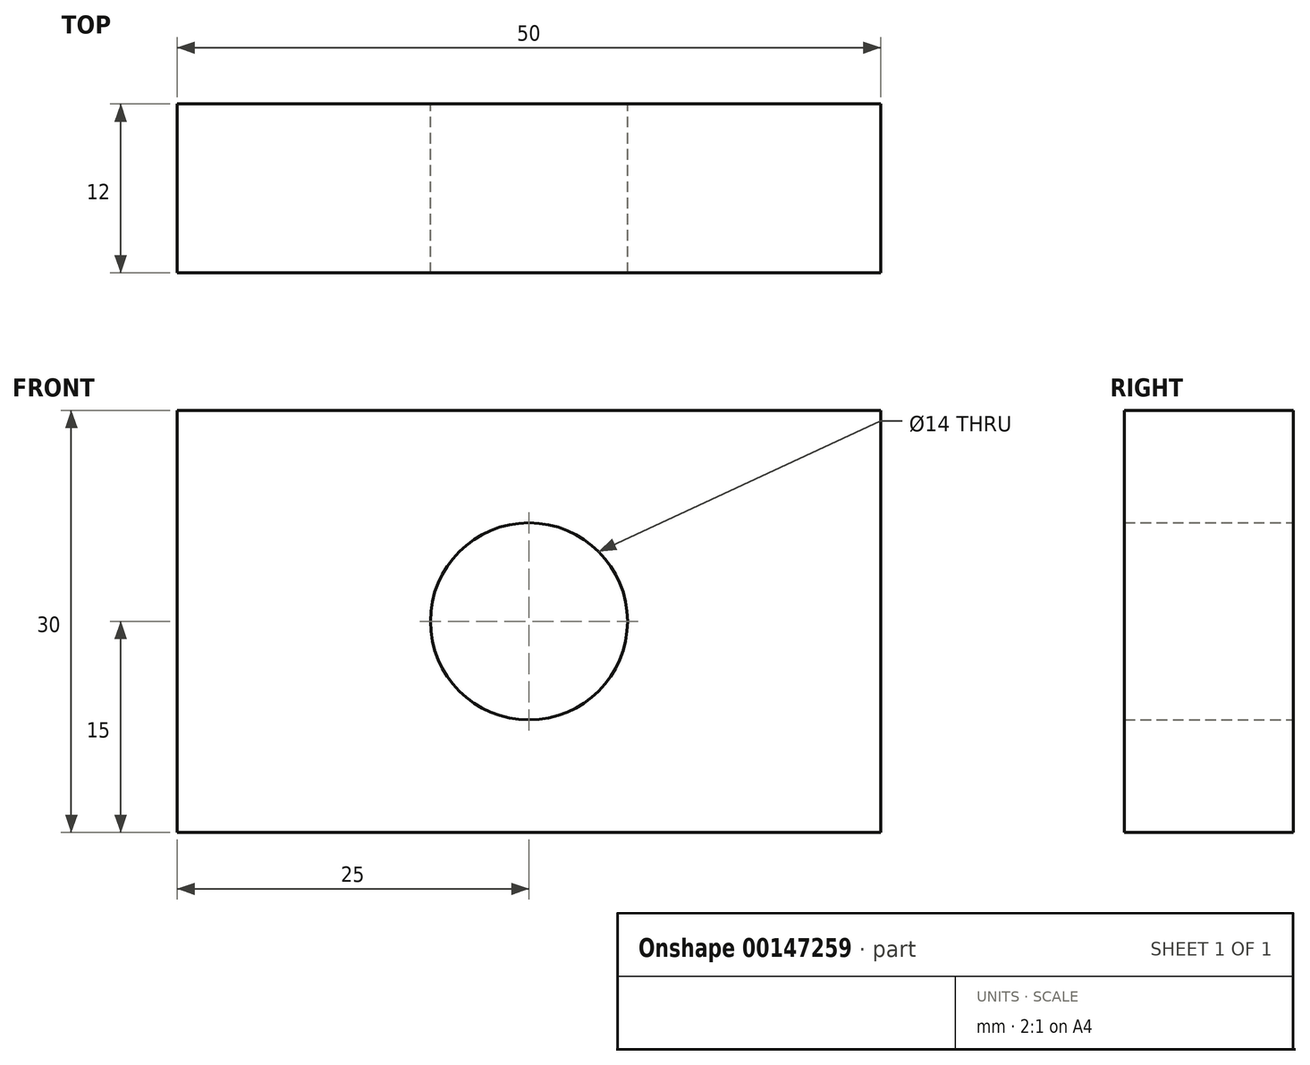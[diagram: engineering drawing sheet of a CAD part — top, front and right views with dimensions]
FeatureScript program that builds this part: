
annotation { "Feature Type Name" : "Feature", "Feature Type Description" : "" }
export const myFeature = defineFeature(function(context is Context, id is Id, definition is map)
    precondition{}
    {
        {
            var Q0;
            Q0=qCreatedBy(makeId("Front.planeOp"),FACE);
            var sketch = newSketch(context, id + "F0", { "sketchPlane" : qUnion([Q0])});
            skLineSegment(sketch, "E0.bottom", {"start": v(-25, 15) * mm, "end": v(25, 15) * mm});
            skLineSegment(sketch, "E0.top", {"start": v(-25, -15) * mm, "end": v(25, -15) * mm});
            skLineSegment(sketch, "E0.left", {"start": v(-25, 15) * mm, "end": v(-25, -15) * mm});
            skLineSegment(sketch, "E0.right", {"start": v(25, 15) * mm, "end": v(25, -15) * mm});
            skPoint(sketch, "E0.middle", {"position": v(0, 0) * mm});
            skCircle(sketch, "E1", {"center": v(0, 0) * mm, "radius": 7 * mm});
            skSolve(sketch);
        }
        {
            var Q0;
            Q0 = qSketchRegion(id + "F0", true);
            extrude(context, id + "F1", {"entities" : qUnion([Q0]), "endBound" : BoundingType.SYMMETRIC, "depth" : 12 * mm});
        }
    });
